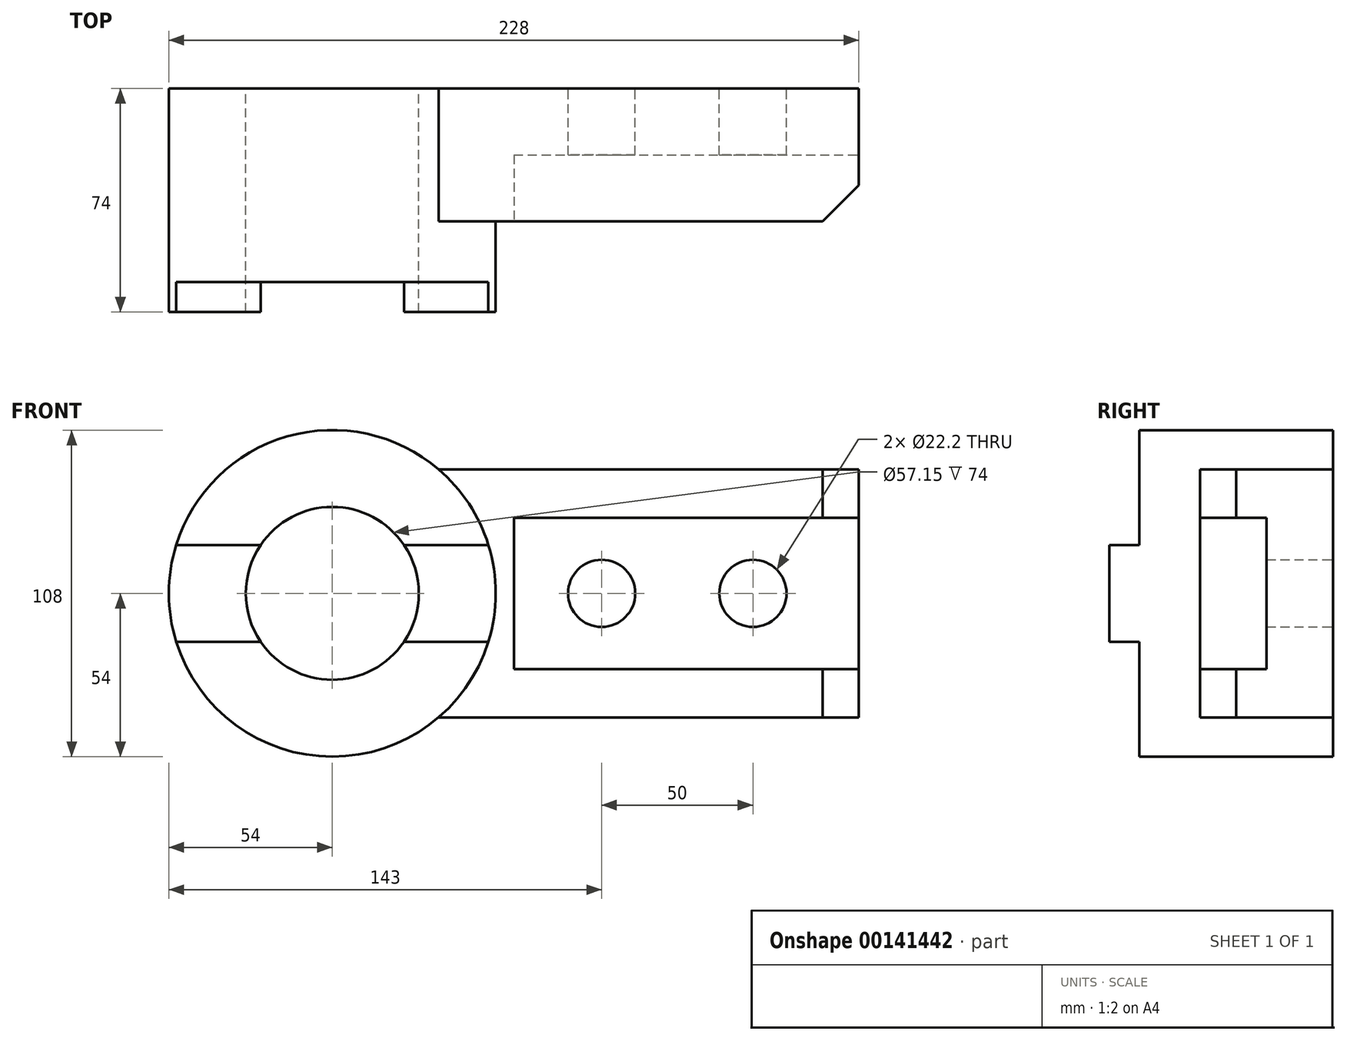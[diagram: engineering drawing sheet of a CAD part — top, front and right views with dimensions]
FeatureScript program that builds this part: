
annotation { "Feature Type Name" : "Feature", "Feature Type Description" : "" }
export const myFeature = defineFeature(function(context is Context, id is Id, definition is map)
    precondition{}
    {
        {
            var Q0;
            Q0=qCreatedBy(makeId("Front.planeOp"),FACE);
            var sketch = newSketch(context, id + "F0", { "sketchPlane" : qUnion([Q0])});
            skCircle(sketch, "E0", {"center": v(0, 0) * mm, "radius": 54 * mm});
            skCircle(sketch, "E1", {"center": v(0, 0) * mm, "radius": 28.57 * mm});
            skLineSegment(sketch, "E2", {"start": v(35.14, 41) * mm, "end": v(174, 41) * mm});
            skLineSegment(sketch, "E3", {"start": v(174, 41) * mm, "end": v(174, -41) * mm});
            skLineSegment(sketch, "E4", {"start": v(174, -41) * mm, "end": v(35.14, -41) * mm});
            skCircle(sketch, "E5", {"center": v(139, 0) * mm, "radius": 11.1 * mm});
            skCircle(sketch, "E6", {"center": v(89, 0) * mm, "radius": 11.1 * mm});
            skSolve(sketch);
        }
        {
            var Q0;
            Q0=makeQuery(id+"F0.imprint","IMPRINT",FACE,{"disambiguationData":[TD([[makeQuery(id+"F0.imprint","IMPRINT",EDGE,{"derivedFrom":sQuery(id+"F0.wireOp",EDGE,"E1")}),-1.0]])]});
            extrude(context, id + "F1", {"entities" : qUnion([Q0]), "depth" : 64 * mm});
        }
        {
            var Q0;
            {var subQ1=sQuery(id+"F0.wireOp",EDGE,"E2");Q0=makeQuery(id+"F0.imprint","IMPRINT",FACE,{"disambiguationData":[TD([[makeQuery(id+"F0.imprint","IMPRINT",EDGE,{"derivedFrom":subQ1}),-1.0]])]});}
            extrude(context, id + "F2", {"entities" : qUnion([Q0]), "operationType" : NewBodyOperationType.ADD, "depth" : 44 * mm});
        }
        {
            var Q0;
            Q0=makeQuery(id+"F2.opExtrude","CAP_FACE",FACE,{"disambiguationData":[OSD([sQuery(id+"F0.wireOp",EDGE,"E0"),sQuery(id+"F0.wireOp",EDGE,"E2"),sQuery(id+"F0.wireOp",EDGE,"E3"),sQuery(id+"F0.wireOp",EDGE,"E4"),sQuery(id+"F0.wireOp",EDGE,"E5"),sQuery(id+"F0.wireOp",EDGE,"E6")])],"isStart":false});
            var sketch = newSketch(context, id + "F3", { "sketchPlane" : qUnion([Q0])});
            skLineSegment(sketch, "E7.bottom", {"start": v(60, 25) * mm, "end": v(174, 25) * mm});
            skLineSegment(sketch, "E7.top", {"start": v(60, -25) * mm, "end": v(174, -25) * mm});
            skLineSegment(sketch, "E7.left", {"start": v(60, 25) * mm, "end": v(60, -25) * mm});
            skLineSegment(sketch, "E7.right", {"start": v(174, 25) * mm, "end": v(174, -25) * mm});
            skSolve(sketch);
        }
        {
            var Q0;
            Q0 = qSketchRegion(id + "F3", true);
            extrude(context, id + "F4", {"entities" : qUnion([Q0]), "operationType" : NewBodyOperationType.REMOVE, "oppositeDirection" : true, "depth" : 22 * mm});
        }
        {
            var Q0;
            {var subQ0=sQuery(id+"F0.wireOp",EDGE,"E4");var subQ1=sQuery(id+"F0.wireOp",EDGE,"E3");Q0=makeQuery(id+"F4.boolean.opBoolean","SPLIT",EDGE,{"disambiguationData":[TD([makeQuery(id+"F2.opExtrude","SWEPT_FACE",FACE,{"disambiguationData":[OSD([subQ0])]})])],"derivedFrom":makeQuery(id+"F2.opExtrude","CAP_EDGE",EDGE,{"disambiguationData":[OSD([subQ1])],"isStart":false})});}
            chamfer(context, id + "F5", {"entities" : qUnion([Q0]), "width" : 12 * mm, "tangentPropagation" : true});
        }
        {
            var Q0;
            Q0=makeQuery(id+"F1.opExtrude","CAP_FACE",FACE,{"disambiguationData":[OSD([sQuery(id+"F0.wireOp",EDGE,"E0"),sQuery(id+"F0.wireOp",EDGE,"E1")])],"isStart":false});
            var sketch = newSketch(context, id + "F6", { "sketchPlane" : qUnion([Q0])});
            skLineSegment(sketch, "E8", {"start": v(-51.58, 16) * mm, "end": v(-23.68, 16) * mm});
            skLineSegment(sketch, "E9", {"start": v(-51.58, -16) * mm, "end": v(-23.68, -16) * mm});
            skArc(sketch, "E10", {"start": v(-23.68, 16) * mm, "mid": v(-28.57, 0) * mm, "end": v(-23.68, -16) * mm});
            skArc(sketch, "E11", {"start": v(-51.58, 16) * mm, "mid": v(-54, 0) * mm, "end": v(-51.58, -16) * mm});
            skArc(sketch, "E12.MirrorCS", {"start": v(-23.68, -16) * mm, "mid": v(-28.58, 0) * mm, "end": v(-23.68, 16) * mm});
            skArc(sketch, "E13.MirrorCS", {"start": v(-51.58, -16) * mm, "mid": v(-54, 0) * mm, "end": v(-51.58, 16) * mm});
            skArc(sketch, "E14.MirrorCS", {"start": v(-23.68, 16) * mm, "mid": v(-28.58, 0) * mm, "end": v(-23.68, -16) * mm});
            skArc(sketch, "E15.MirrorCS", {"start": v(23.68, 16) * mm, "mid": v(28.58, 0) * mm, "end": v(23.68, -16) * mm});
            skLineSegment(sketch, "E16.MirrorCS", {"start": v(51.58, 16) * mm, "end": v(23.68, 16) * mm});
            skLineSegment(sketch, "E17.MirrorCS", {"start": v(51.58, -16) * mm, "end": v(23.68, -16) * mm});
            skArc(sketch, "E18.MirrorCS", {"start": v(51.58, -16) * mm, "mid": v(54, 0) * mm, "end": v(51.58, 16) * mm});
            skSolve(sketch);
        }
        {
            var Q0;
            Q0 = qSketchRegion(id + "F6", true);
            extrude(context, id + "F7", {"entities" : qUnion([Q0]), "operationType" : NewBodyOperationType.ADD, "depth" : 10 * mm});
        }
        {
            var Q0;
            {var subQ0=sQuery(id+"F0.wireOp",EDGE,"E3");var subQ1=sQuery(id+"F0.wireOp",EDGE,"E2");Q0=makeQuery(id+"F4.boolean.opBoolean","SPLIT",EDGE,{"disambiguationData":[TD([makeQuery(id+"F2.opExtrude","SWEPT_FACE",FACE,{"disambiguationData":[OSD([subQ1])]})])],"derivedFrom":makeQuery(id+"F2.opExtrude","CAP_EDGE",EDGE,{"disambiguationData":[OSD([subQ0])],"isStart":false})});}
            chamfer(context, id + "F8", {"entities" : qUnion([Q0]), "width" : 12 * mm, "tangentPropagation" : true});
        }
    });
